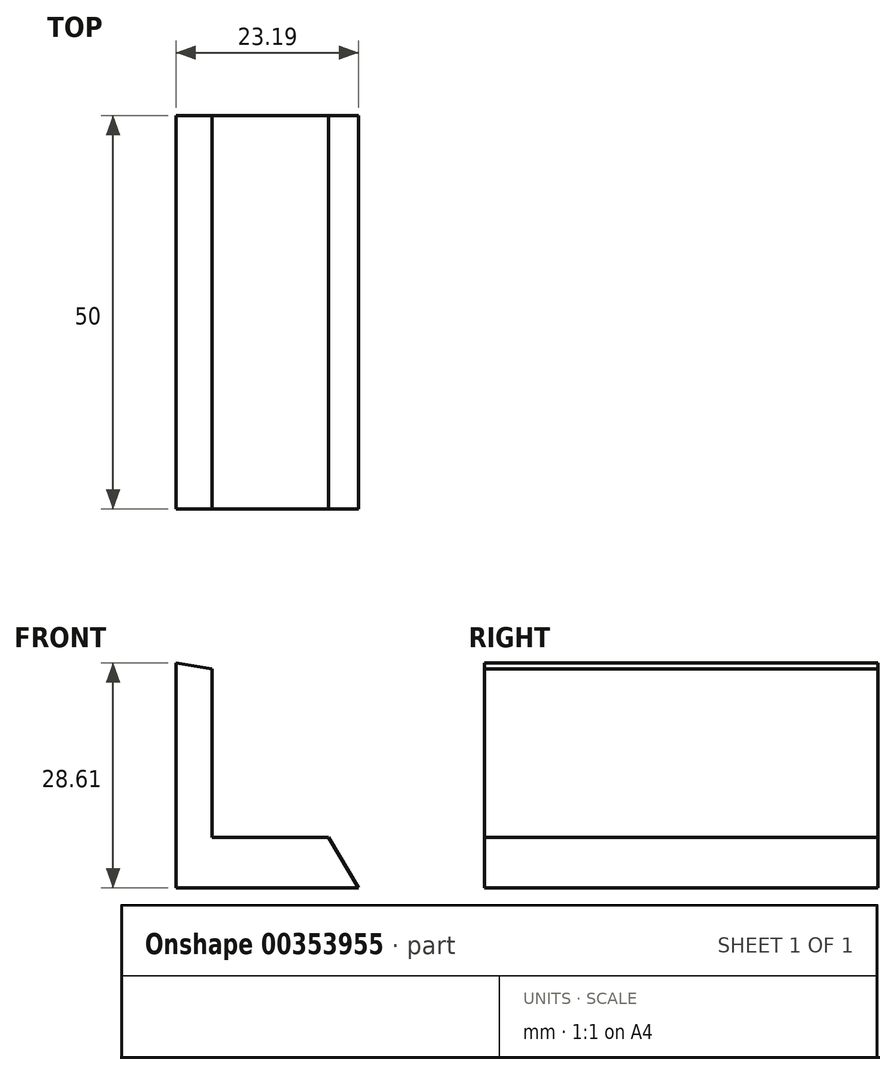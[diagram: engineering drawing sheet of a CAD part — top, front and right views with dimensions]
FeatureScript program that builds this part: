
annotation { "Feature Type Name" : "Feature", "Feature Type Description" : "" }
export const myFeature = defineFeature(function(context is Context, id is Id, definition is map)
    precondition{}
    {
        {
            var Q0;
            Q0=qCreatedBy(makeId("Front.planeOp"),FACE);
            var sketch = newSketch(context, id + "F0", { "sketchPlane" : qUnion([Q0])});
            skLineSegment(sketch, "E0", {"start": v(-38.38, 13.62) * mm, "end": v(-38.38, -15) * mm});
            skLineSegment(sketch, "E1", {"start": v(-15.2, -15) * mm, "end": v(-18.99, -8.55) * mm});
            skLineSegment(sketch, "E2", {"start": v(-18.99, -8.55) * mm, "end": v(-33.78, -8.55) * mm});
            skLineSegment(sketch, "E3", {"start": v(-33.78, -8.55) * mm, "end": v(-33.78, 12.82) * mm});
            skLineSegment(sketch, "E4", {"start": v(-33.78, 12.82) * mm, "end": v(-38.38, 13.62) * mm});
            skLineSegment(sketch, "E5", {"start": v(-38.38, -15) * mm, "end": v(-15.2, -15) * mm});
            skSolve(sketch);
        }
        {
            var Q0;
            Q0 = qSketchRegion(id + "F0", true);
            extrude(context, id + "F1", {"entities" : qUnion([Q0]), "endBound" : BoundingType.SYMMETRIC, "depth" : 50 * mm});
        }
    });
